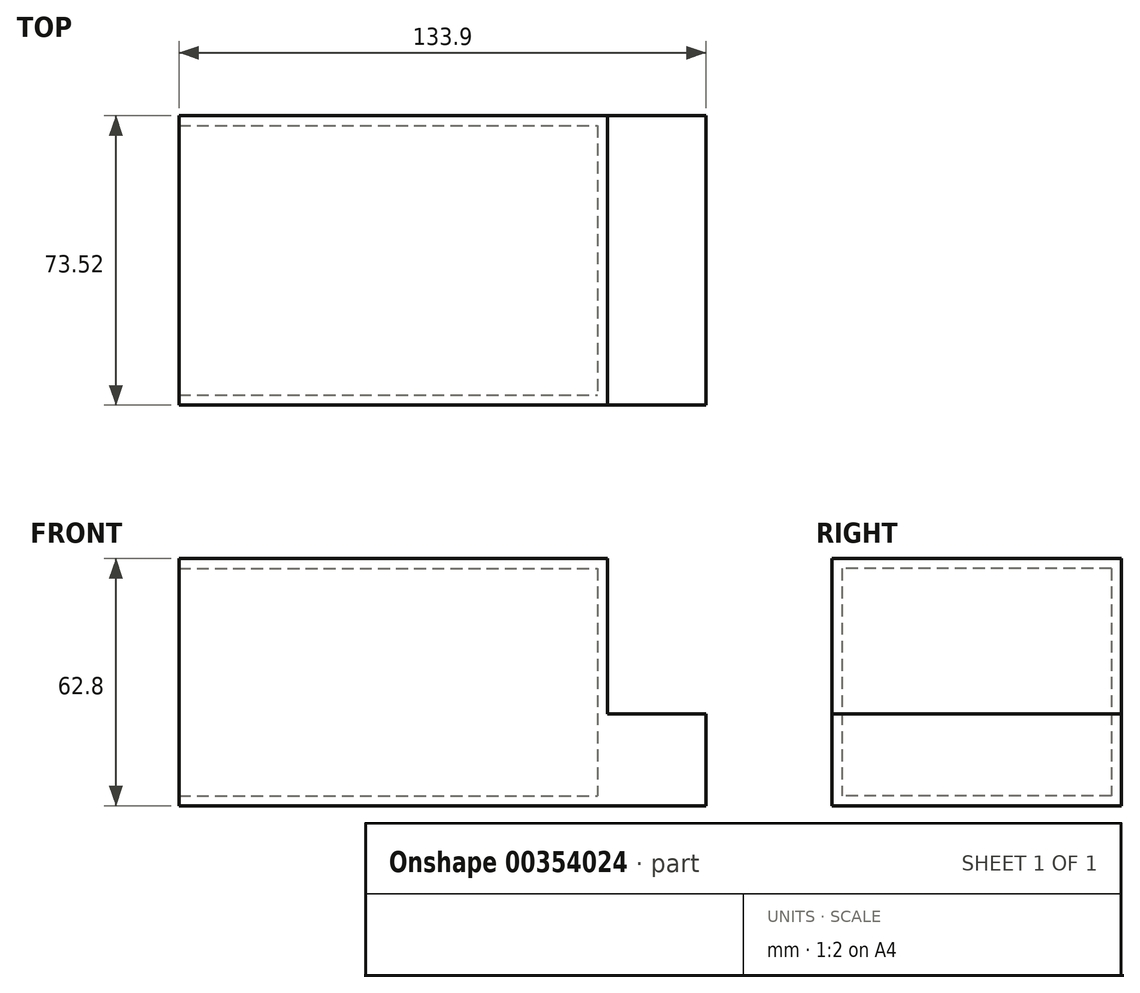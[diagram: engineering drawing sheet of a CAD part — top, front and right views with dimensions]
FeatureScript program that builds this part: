
annotation { "Feature Type Name" : "Feature", "Feature Type Description" : "" }
export const myFeature = defineFeature(function(context is Context, id is Id, definition is map)
    precondition{}
    {
        {
            var Q0;
            Q0=qCreatedBy(makeId("Top.planeOp"),FACE);
            var sketch = newSketch(context, id + "F0", { "sketchPlane" : qUnion([Q0])});
            skLineSegment(sketch, "E0.bottom", {"start": v(-46.66, 31.99) * mm, "end": v(62.24, 31.99) * mm});
            skLineSegment(sketch, "E0.top", {"start": v(-46.66, -41.53) * mm, "end": v(62.24, -41.53) * mm});
            skLineSegment(sketch, "E0.left", {"start": v(-46.66, 31.99) * mm, "end": v(-46.66, -41.53) * mm});
            skLineSegment(sketch, "E0.right", {"start": v(62.24, 31.99) * mm, "end": v(62.24, -41.53) * mm});
            skSolve(sketch);
        }
        {
            var Q0;
            Q0 = qSketchRegion(id + "F0", true);
            extrude(context, id + "F1", {"entities" : qUnion([Q0]), "depth" : 62.8 * mm});
        }
        {
            var Q0;
            Q0=makeQuery(id+"F1.opExtrude","SWEPT_FACE",FACE,{"disambiguationData":[OSD([sQuery(id+"F0.wireOp",EDGE,"E0.left")])]});
            shell(context, id + "F2", {"entities" : qUnion([Q0]), "thickness" : 2.5 * mm});
        }
        {
            var Q0;
            Q0=makeQuery(id+"F1.opExtrude","SWEPT_FACE",FACE,{"disambiguationData":[OSD([sQuery(id+"F0.wireOp",EDGE,"E0.right")])]});
            var sketch = newSketch(context, id + "F3", { "sketchPlane" : qUnion([Q0])});
            skLineSegment(sketch, "E1.bottom", {"start": v(-41.53, 23.28) * mm, "end": v(31.99, 23.28) * mm});
            skLineSegment(sketch, "E1.top", {"start": v(-41.53, 0) * mm, "end": v(31.99, 0) * mm});
            skLineSegment(sketch, "E1.left", {"start": v(-41.53, 23.28) * mm, "end": v(-41.53, 0) * mm});
            skLineSegment(sketch, "E1.right", {"start": v(31.99, 23.28) * mm, "end": v(31.99, 0) * mm});
            skSolve(sketch);
        }
        {
            var Q0;
            Q0 = qSketchRegion(id + "F3", true);
            extrude(context, id + "F4", {"entities" : qUnion([Q0]), "operationType" : NewBodyOperationType.ADD, "depth" : 25 * mm});
        }
        {
            var Q0;
            Q0=makeQuery(id+"F2.opShell","OFFSET_FACE",FACE,{"disambiguationData":[OSD([sQuery(id+"F0.wireOp",EDGE,"E0.right")])]});
            var sketch = newSketch(context, id + "F5", { "sketchPlane" : qUnion([Q0])});
            skLineSegment(sketch, "E2.bottom", {"start": v(-17.17, 50.95) * mm, "end": v(-5.1, 50.95) * mm});
            skLineSegment(sketch, "E2.top", {"start": v(-17.17, 44.42) * mm, "end": v(-5.1, 44.42) * mm});
            skLineSegment(sketch, "E2.left", {"start": v(-17.17, 50.95) * mm, "end": v(-17.17, 44.42) * mm});
            skLineSegment(sketch, "E2.right", {"start": v(-5.1, 50.95) * mm, "end": v(-5.1, 44.42) * mm});
            skLineSegment(sketch, "E3.MirrorCS", {"start": v(5.1, 50.95) * mm, "end": v(5.1, 44.42) * mm});
            skLineSegment(sketch, "E4.MirrorCS", {"start": v(17.17, 44.42) * mm, "end": v(5.1, 44.42) * mm});
            skLineSegment(sketch, "E5.MirrorCS", {"start": v(17.17, 50.95) * mm, "end": v(5.1, 50.95) * mm});
            skLineSegment(sketch, "E6.MirrorCS", {"start": v(17.17, 50.95) * mm, "end": v(17.17, 44.42) * mm});
            skSolve(sketch);
        }
        {
            var Q0;
            Q0 = qSketchRegion(id + "F5", true);
            extrude(context, id + "F6", {"entities" : qUnion([Q0]), "operationType" : NewBodyOperationType.ADD, "depth" : -.9 * mm});
        }
    });
